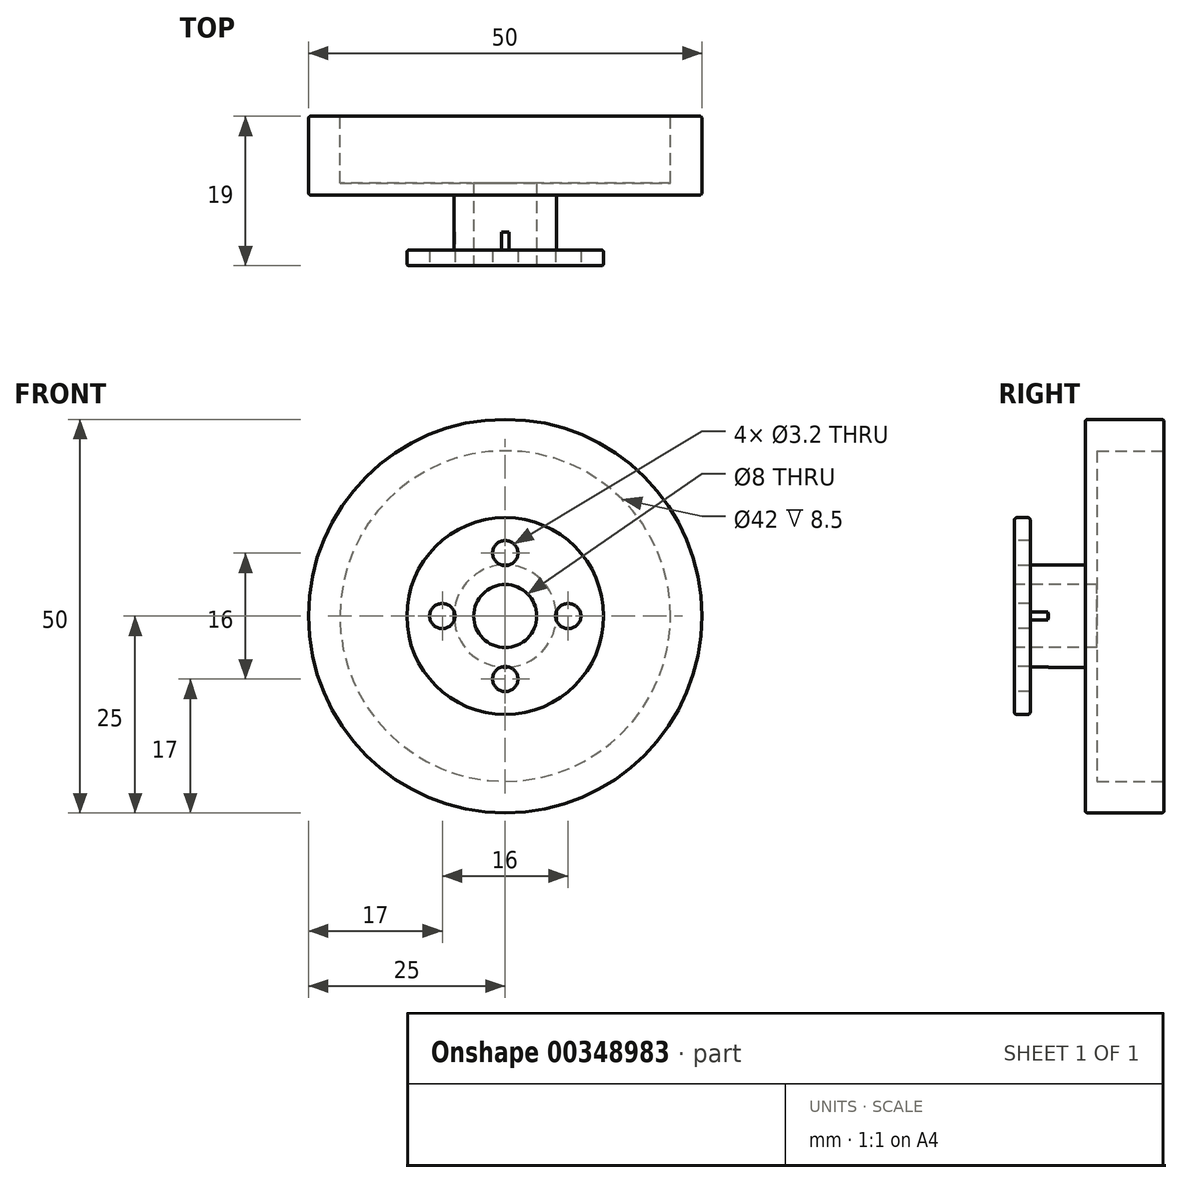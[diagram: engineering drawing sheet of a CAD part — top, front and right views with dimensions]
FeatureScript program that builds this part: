
annotation { "Feature Type Name" : "Feature", "Feature Type Description" : "" }
export const myFeature = defineFeature(function(context is Context, id is Id, definition is map)
    precondition{}
    {
        {
            var Q0;
            Q0=qCreatedBy(makeId("Front.planeOp"),FACE);
            var sketch = newSketch(context, id + "F0", { "sketchPlane" : qUnion([Q0])});
            skCircle(sketch, "E0", {"center": v(0, 0) * mm, "radius": 25 * mm});
            skSolve(sketch);
        }
        {
            var Q0;
            Q0 = qSketchRegion(id + "F0", true);
            extrude(context, id + "F1", {"entities" : qUnion([Q0]), "depth" : 10 * mm});
        }
        {
            var Q0;
            Q0=makeQuery(id+"F1.opExtrude","CAP_FACE",FACE,{"disambiguationData":[OSD([sQuery(id+"F0.wireOp",EDGE,"E0")])],"isStart":false});
            var sketch = newSketch(context, id + "F2", { "sketchPlane" : qUnion([Q0])});
            skCircle(sketch, "E1", {"center": v(0, 0) * mm, "radius": 6.5 * mm});
            skSolve(sketch);
        }
        {
            var Q0;
            Q0 = qSketchRegion(id + "F2", true);
            extrude(context, id + "F3", {"entities" : qUnion([Q0]), "operationType" : NewBodyOperationType.ADD, "depth" : 7 * mm});
        }
        {
            var Q0;
            Q0=makeQuery(id+"F3.opExtrude","CAP_FACE",FACE,{"disambiguationData":[OSD([sQuery(id+"F2.wireOp",EDGE,"E1")])],"isStart":false});
            var sketch = newSketch(context, id + "F4", { "sketchPlane" : qUnion([Q0])});
            skCircle(sketch, "E2", {"center": v(0, 0) * mm, "radius": 12.5 * mm});
            skSolve(sketch);
        }
        {
            var Q0;
            Q0 = qSketchRegion(id + "F4", true);
            extrude(context, id + "F5", {"entities" : qUnion([Q0]), "operationType" : NewBodyOperationType.ADD, "depth" : 2 * mm});
        }
        {
            var Q0;
            Q0=makeQuery(id+"F5.opExtrude","CAP_FACE",FACE,{"disambiguationData":[OSD([sQuery(id+"F4.wireOp",EDGE,"E2")])],"isStart":false});
            var sketch = newSketch(context, id + "F6", { "sketchPlane" : qUnion([Q0])});
            skCircle(sketch, "E3", {"center": v(0, 0) * mm, "radius": 4 * mm});
            skSolve(sketch);
        }
        {
            var Q0;
            Q0=makeQuery(id+"F6.imprint","IMPRINT",FACE,{"disambiguationData":[TD([[makeQuery(id+"F6.imprint","IMPRINT",EDGE,{"derivedFrom":sQuery(id+"F6.wireOp",EDGE,"E3")}),1.0]])]});
            extrude(context, id + "F7", {"entities" : qUnion([Q0]), "operationType" : NewBodyOperationType.REMOVE, "endBound" : BoundingType.THROUGH_ALL, "oppositeDirection" : true, "depth" : 25 * mm});
        }
        {
            var Q0;
            Q0=makeQuery(id+"F5.opExtrude","CAP_FACE",FACE,{"disambiguationData":[OSD([sQuery(id+"F4.wireOp",EDGE,"E2")])],"isStart":false});
            var sketch = newSketch(context, id + "F8", { "sketchPlane" : qUnion([Q0])});
            skCircle(sketch, "E4", {"center": v(0, 0) * mm, "radius": 8 * mm, "construction": true});
            skCircle(sketch, "E5", {"center": v(0, 8) * mm, "radius": 1.65 * mm});
            skCircle(sketch, "E6", {"center": v(0, -8) * mm, "radius": 1.65 * mm});
            skCircle(sketch, "E7", {"center": v(8, 0) * mm, "radius": 1.2 * mm});
            skCircle(sketch, "E8", {"center": v(-8, 0) * mm, "radius": 1.65 * mm});
            skSolve(sketch);
        }
        {
            var Q0;
            Q0=sQuery(id+"F8.wireOp",VERTEX,"E8.center");
            var Q1;
            Q1=sQuery(id+"F8.wireOp",VERTEX,"E5.center");
            var Q2;
            Q2=sQuery(id+"F8.wireOp",VERTEX,"E7.center");
            var Q3;
            Q3=sQuery(id+"F8.wireOp",VERTEX,"E6.center");
            var Q4;
            Q4=makeQuery(id+"F1.opExtrude","SWEPT_BODY",BODY,{"disambiguationData":[OSD([sQuery(id+"F0.wireOp",EDGE,"E0")])]});
            hole(context, id + "F9", {"style" : HoleStyle.SIMPLE, "endStyle" : HoleEndStyle.BLIND, "standardTappedOrClearance" : lookupTablePath({ "standard" : "ISO", "engagement" : "75%", "pitch" : "0.75 mm", "size" : "M4", "type" : "Tapped" }), "standardBlindInLast" : lookupTablePath({ "standard" : "ISO", "engagement" : "75%", "pitch" : "0.75 mm", "size" : "M4", "type" : "Tapped" }), "holeDiameter" : 3.2 * mm, "showTappedDepth" : true, "holeDepth" : 4.25 * mm, "isTappedThrough" : true, "tappedDepth" : 2.75 * mm, "tapClearance" : 2, "startFromSketch" : true, "locations" : qUnion([Q0, Q1, Q2, Q3]), "scope" : qUnion([Q4])});
        }
        {
            var Q0;
            Q0=makeQuery(id+"F1.opExtrude","CAP_EDGE",EDGE,{"disambiguationData":[OSD([sQuery(id+"F0.wireOp",EDGE,"E0")])],"isStart":false});
            var Q1;
            Q1=makeQuery(id+"F1.opExtrude","CAP_EDGE",EDGE,{"disambiguationData":[OSD([sQuery(id+"F0.wireOp",EDGE,"E0")])],"isStart":true});
            var Q2;
            Q2=makeQuery(id+"F5.opExtrude","CAP_EDGE",EDGE,{"disambiguationData":[OSD([sQuery(id+"F4.wireOp",EDGE,"E2")])],"isStart":false});
            var Q3;
            Q3=makeQuery(id+"F5.opExtrude","CAP_EDGE",EDGE,{"disambiguationData":[OSD([sQuery(id+"F4.wireOp",EDGE,"E2")])],"isStart":true});
            var Q4;
            Q4=makeQuery(id+"F7.boolean.opBoolean","COPY",EDGE,{"derivedFrom":makeQuery(id+"F7.opExtrude","CAP_EDGE",EDGE,{"disambiguationData":[OSD([sQuery(id+"F6.wireOp",EDGE,"E3")])],"isStart":true})});
            fillet(context, id + "F10", {"entities" : qUnion([Q0, Q1, Q2, Q3, Q4]), "radius" : 0.3 * mm, "tangentPropagation" : true, "allowEdgeOverflow" : false});
        }
        {
            var Q0;
            Q0=makeQuery(id+"F1.opExtrude","CAP_FACE",FACE,{"disambiguationData":[OSD([sQuery(id+"F0.wireOp",EDGE,"E0")])],"isStart":true});
            var sketch = newSketch(context, id + "F11", { "sketchPlane" : qUnion([Q0])});
            skCircle(sketch, "E9", {"center": v(0, 0) * mm, "radius": 21 * mm});
            skSolve(sketch);
        }
        {
            var Q0;
            Q0=makeQuery(id+"F11.imprint","IMPRINT",FACE,{"disambiguationData":[TD([[makeQuery(id+"F11.imprint","IMPRINT",EDGE,{"derivedFrom":sQuery(id+"F11.wireOp",EDGE,"E9")}),1.0]])]});
            extrude(context, id + "F12", {"entities" : qUnion([Q0]), "operationType" : NewBodyOperationType.REMOVE, "oppositeDirection" : true, "depth" : 8.5 * mm});
        }
    });
